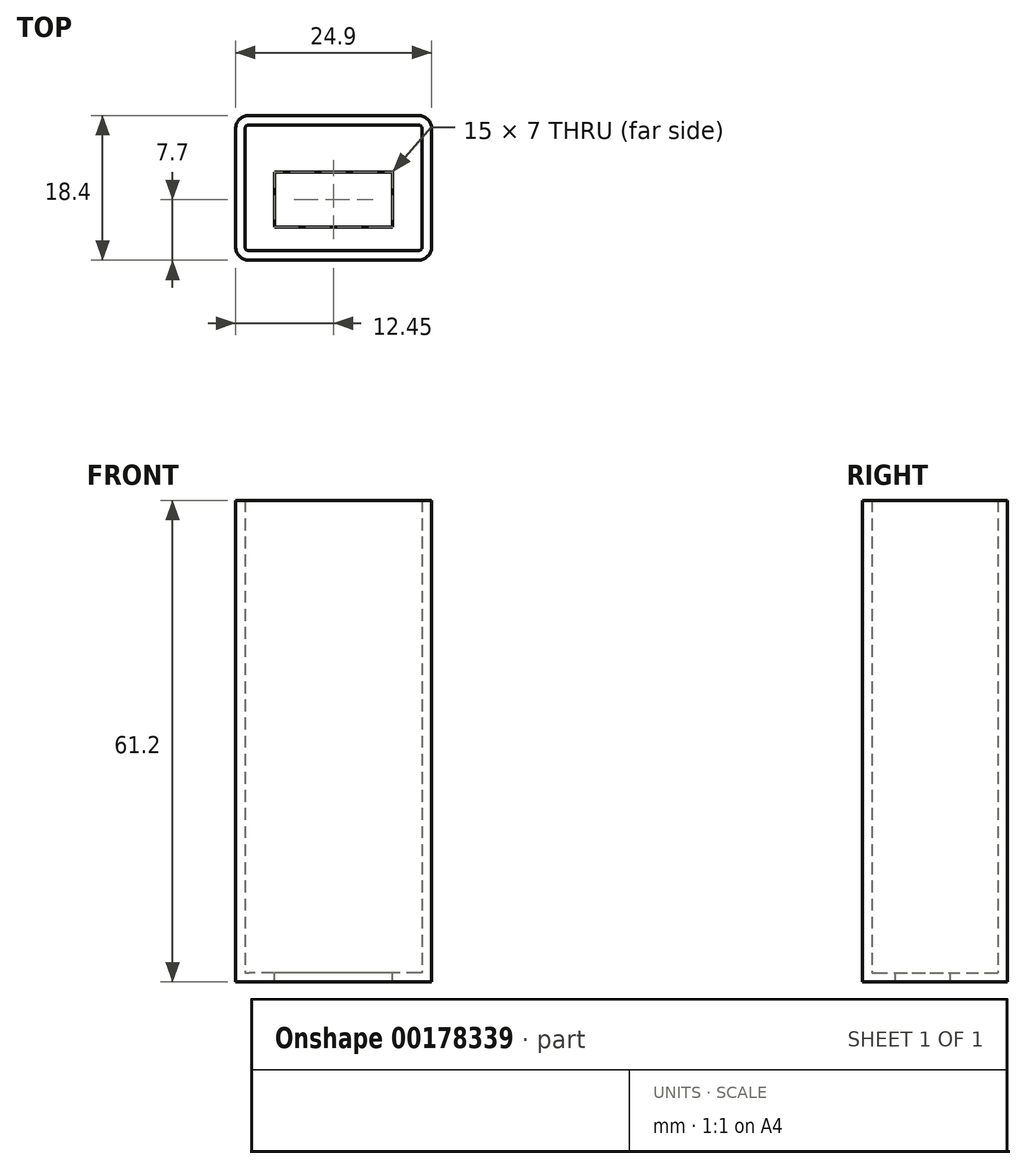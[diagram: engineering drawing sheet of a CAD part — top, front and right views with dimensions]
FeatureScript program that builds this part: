
annotation { "Feature Type Name" : "Feature", "Feature Type Description" : "" }
export const myFeature = defineFeature(function(context is Context, id is Id, definition is map)
    precondition{}
    {
        {
            var Q0;
            Q0=qCreatedBy(makeId("Top.planeOp"),FACE);
            var sketch = newSketch(context, id + "F0", { "sketchPlane" : qUnion([Q0])});
            skLineSegment(sketch, "E0.bottom", {"start": v(10.75, -8) * mm, "end": v(-10.75, -8) * mm});
            skLineSegment(sketch, "E0.top", {"start": v(10.75, 8) * mm, "end": v(-10.75, 8) * mm});
            skLineSegment(sketch, "E0.left", {"start": v(11.25, -7.5) * mm, "end": v(11.25, 7.5) * mm});
            skLineSegment(sketch, "E0.right", {"start": v(-11.25, -7.5) * mm, "end": v(-11.25, 7.5) * mm});
            skPoint(sketch, "E0.middle", {"position": v(0, 0) * mm});
            skPoint(sketch, "E1.visualSharp", {"position": v(-11.25, 8) * mm});
            skArc(sketch, "E1.filletArc", {"start": v(-10.75, 8) * mm, "mid": v(-11.1, 7.85) * mm, "end": v(-11.25, 7.5) * mm});
            skPoint(sketch, "E2.visualSharp", {"position": v(11.25, 8) * mm});
            skArc(sketch, "E2.filletArc", {"start": v(11.25, 7.5) * mm, "mid": v(11.1, 7.85) * mm, "end": v(10.75, 8) * mm});
            skPoint(sketch, "E3.visualSharp", {"position": v(11.25, -8) * mm});
            skArc(sketch, "E3.filletArc", {"start": v(10.75, -8) * mm, "mid": v(11.1, -7.85) * mm, "end": v(11.25, -7.5) * mm});
            skPoint(sketch, "E4.visualSharp", {"position": v(-11.25, -8) * mm});
            skArc(sketch, "E4.filletArc", {"start": v(-11.25, -7.5) * mm, "mid": v(-11.1, -7.85) * mm, "end": v(-10.75, -8) * mm});
            skArc(sketch, "E5.0", {"start": v(-12.45, -7.5) * mm, "mid": v(-11.95, -8.7) * mm, "end": v(-10.75, -9.2) * mm});
            skLineSegment(sketch, "E5.1", {"start": v(10.75, -9.2) * mm, "end": v(-10.75, -9.2) * mm});
            skLineSegment(sketch, "E5.2", {"start": v(-12.45, -7.5) * mm, "end": v(-12.45, 7.5) * mm});
            skArc(sketch, "E5.3", {"start": v(10.75, -9.2) * mm, "mid": v(11.95, -8.7) * mm, "end": v(12.45, -7.5) * mm});
            skArc(sketch, "E5.4", {"start": v(-10.75, 9.2) * mm, "mid": v(-11.95, 8.7) * mm, "end": v(-12.45, 7.5) * mm});
            skLineSegment(sketch, "E5.5", {"start": v(10.75, 9.2) * mm, "end": v(-10.75, 9.2) * mm});
            skArc(sketch, "E5.6", {"start": v(12.45, 7.5) * mm, "mid": v(11.95, 8.7) * mm, "end": v(10.75, 9.2) * mm});
            skLineSegment(sketch, "E5.7", {"start": v(12.45, -7.5) * mm, "end": v(12.45, 7.5) * mm});
            skLineSegment(sketch, "E6.bottom", {"start": v(7.5, -5) * mm, "end": v(-7.5, -5) * mm});
            skLineSegment(sketch, "E6.top", {"start": v(7.5, 2) * mm, "end": v(-7.5, 2) * mm});
            skLineSegment(sketch, "E6.left", {"start": v(7.5, -5) * mm, "end": v(7.5, 2) * mm});
            skLineSegment(sketch, "E6.right", {"start": v(-7.5, -5) * mm, "end": v(-7.5, 2) * mm});
            skPoint(sketch, "E6.middle", {"position": v(0, -1.5) * mm});
            skSolve(sketch);
        }
        {
            var Q0;
            Q0=makeQuery(id+"F0.imprint","IMPRINT",FACE,{"disambiguationData":[TD([[makeQuery(id+"F0.imprint","IMPRINT",EDGE,{"derivedFrom":sQuery(id+"F0.wireOp",EDGE,"E0.bottom")}),1.0]])]});
            extrude(context, id + "F1", {"entities" : qUnion([Q0]), "depth" : 60 * mm, "hasSecondDirection" : true, "secondDirectionOppositeDirection" : true, "secondDirectionDepth" : 1.2 * mm});
        }
        {
            var Q0;
            Q0=makeQuery(id+"F0.imprint","IMPRINT",FACE,{"disambiguationData":[TD([[makeQuery(id+"F0.imprint","IMPRINT",EDGE,{"derivedFrom":sQuery(id+"F0.wireOp",EDGE,"E0.bottom")}),-1.0]])]});
            extrude(context, id + "F2", {"entities" : qUnion([Q0]), "operationType" : NewBodyOperationType.ADD, "oppositeDirection" : true, "depth" : 1.2 * mm});
        }
    });
